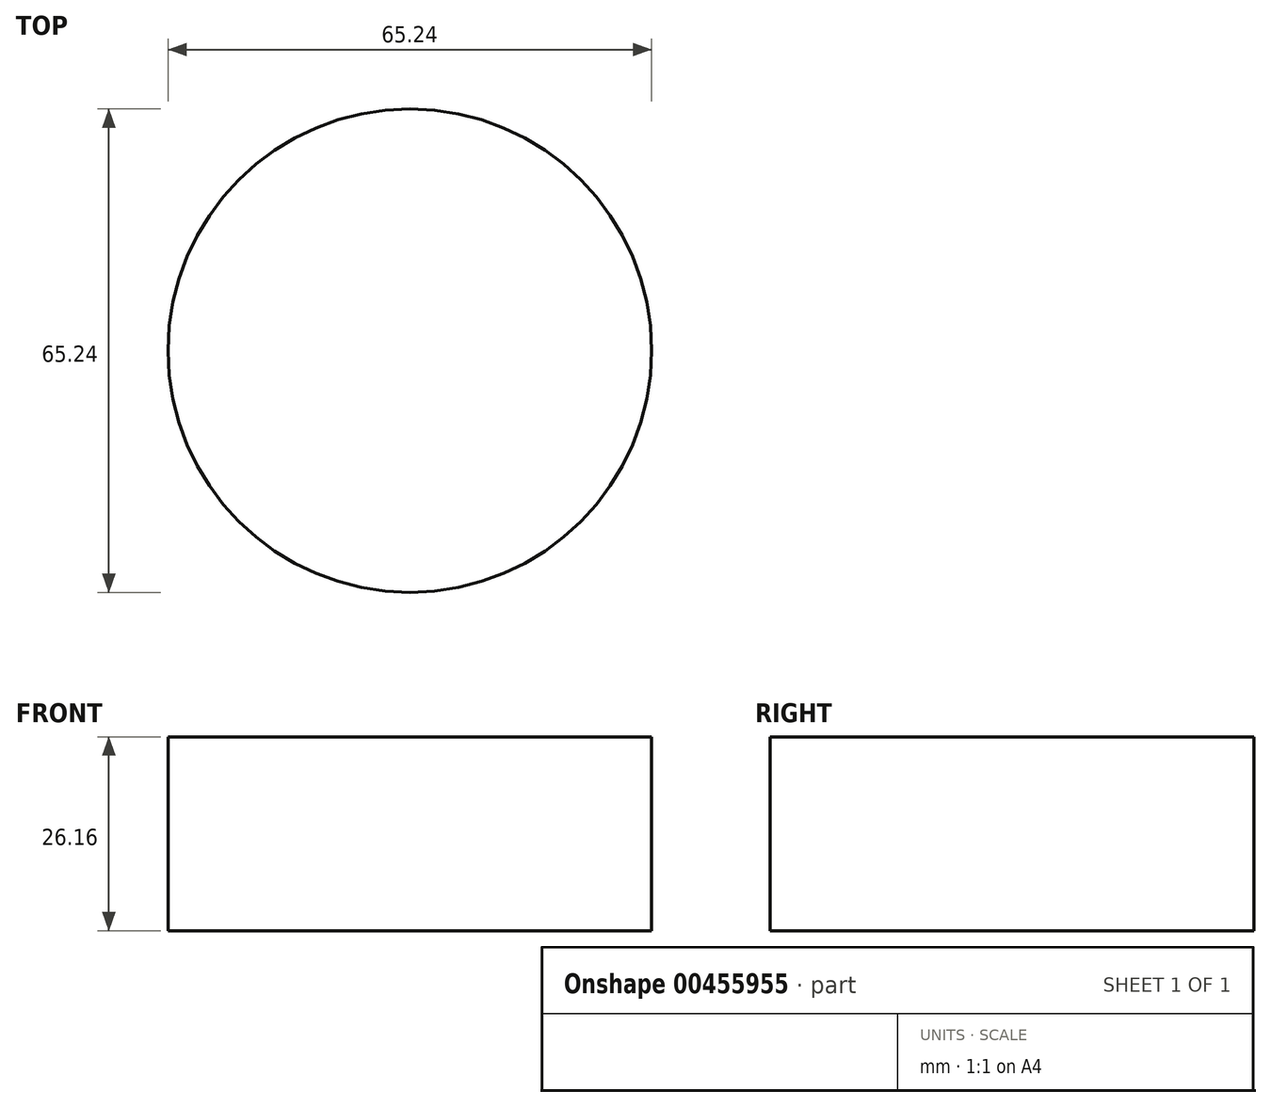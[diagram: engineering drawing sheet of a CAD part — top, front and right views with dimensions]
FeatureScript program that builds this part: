
annotation { "Feature Type Name" : "Feature", "Feature Type Description" : "" }
export const myFeature = defineFeature(function(context is Context, id is Id, definition is map)
    precondition{}
    {
        {
            var Q0;
            Q0=qCreatedBy(makeId("Top.planeOp"),FACE);
            var sketch = newSketch(context, id + "F0", { "sketchPlane" : qUnion([Q0])});
            skCircle(sketch, "E0", {"center": v(0, -1.86) * mm, "radius": 32.62 * mm});
            skSolve(sketch);
        }
        {
            var Q0;
            Q0 = qSketchRegion(id + "F0", true);
            extrude(context, id + "F1", {"entities" : qUnion([Q0]), "depth" : 25.4 * mm});
        }
        {
            var Q0;
            Q0=makeQuery(id+"F0.imprint","IMPRINT",FACE,{"disambiguationData":[TD([[makeQuery(id+"F0.imprint","IMPRINT",EDGE,{"derivedFrom":sQuery(id+"F0.wireOp",EDGE,"E0")}),1.0]])]});
            var Q1;
            Q1=makeQuery(id+"F1.opExtrude","CAP_FACE",FACE,{"disambiguationData":[OSD([sQuery(id+"F0.wireOp",EDGE,"E0")])],"isStart":false});
            extrude(context, id + "F2", {"entities" : qUnion([Q0, Q1]), "operationType" : NewBodyOperationType.ADD, "oppositeDirection" : true, "depth" : 0.76 * mm});
        }
    });
